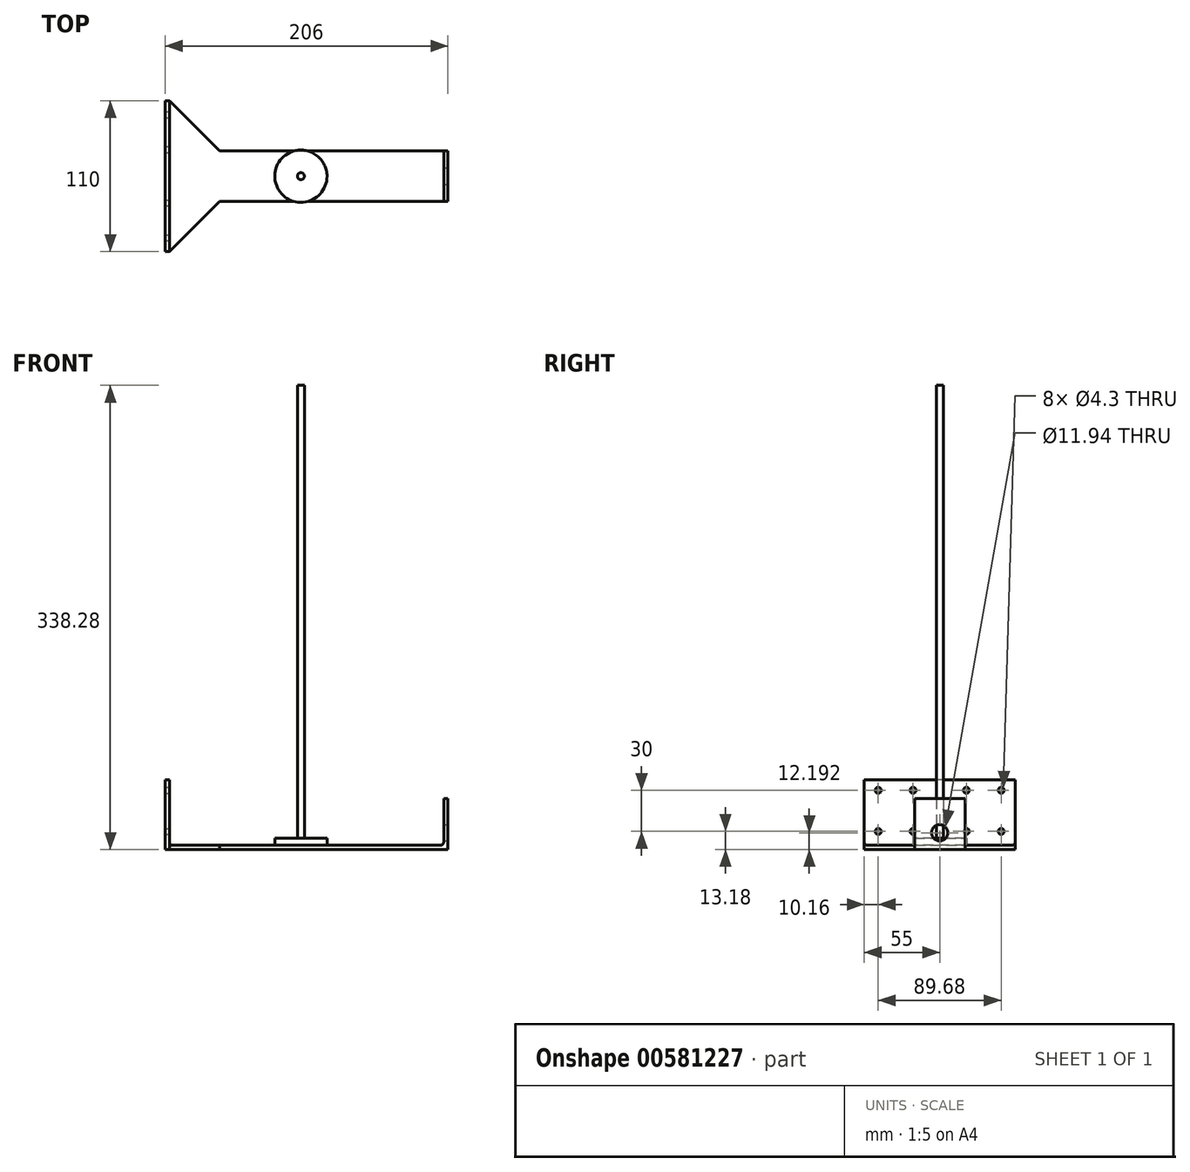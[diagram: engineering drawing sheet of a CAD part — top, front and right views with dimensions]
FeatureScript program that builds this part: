
annotation { "Feature Type Name" : "Feature", "Feature Type Description" : "" }
export const myFeature = defineFeature(function(context is Context, id is Id, definition is map)
    precondition{}
    {
        {
            var Q0;
            Q0=qCreatedBy(makeId("Top.planeOp"),FACE);
            var sketch = newSketch(context, id + "F0", { "sketchPlane" : qUnion([Q0])});
            skLineSegment(sketch, "E0.bottom", {"start": v(1.5, 55) * mm, "end": v(-1.5, 55) * mm});
            skLineSegment(sketch, "E0.top", {"start": v(1.5, -55) * mm, "end": v(-1.5, -55) * mm});
            skLineSegment(sketch, "E0.left", {"start": v(1.5, 55) * mm, "end": v(1.5, -55) * mm});
            skLineSegment(sketch, "E0.right", {"start": v(-1.5, 55) * mm, "end": v(-1.5, -55) * mm});
            skPoint(sketch, "E0.middle", {"position": v(0, 0) * mm});
            skLineSegment(sketch, "E1", {"start": v(1.5, 55) * mm, "end": v(38.09, 18.42) * mm});
            skLineSegment(sketch, "E2", {"start": v(1.5, -55) * mm, "end": v(38.09, -18.42) * mm});
            skLineSegment(sketch, "E3", {"start": v(38.09, 18.41) * mm, "end": v(201.5, 18.41) * mm});
            skLineSegment(sketch, "E4", {"start": v(38.09, -18.42) * mm, "end": v(201.5, -18.42) * mm});
            skLineSegment(sketch, "E5.bottom", {"start": v(201.5, 18.41) * mm, "end": v(204.5, 18.41) * mm});
            skLineSegment(sketch, "E5.top", {"start": v(201.5, -18.42) * mm, "end": v(204.5, -18.42) * mm});
            skLineSegment(sketch, "E5.left", {"start": v(201.5, 18.41) * mm, "end": v(201.5, -18.42) * mm});
            skLineSegment(sketch, "E5.right", {"start": v(204.5, 18.41) * mm, "end": v(204.5, -18.42) * mm});
            skSolve(sketch);
        }
        {
            var Q0;
            Q0=qSketchRegion(id+"F0",true);
            extrude(context, id + "F1", {"entities" : qUnion([Q0]), "depth" : 3 * mm, "offsetDistance" : 25.4 * mm});
        }
        {
            var Q0;
            Q0=makeQuery(id+"F0.imprint","IMPRINT",FACE,{"disambiguationData":[TD([[makeQuery(id+"F0.imprint","IMPRINT",EDGE,{"derivedFrom":sQuery(id+"F0.wireOp",EDGE,"E0.bottom")}),1.0]])]});
            extrude(context, id + "F2", {"entities" : qUnion([Q0]), "operationType" : NewBodyOperationType.ADD, "depth" : 50.8 * mm, "offsetDistance" : 25.4 * mm});
        }
        {
            var Q0;
            Q0=makeQuery(id+"F0.imprint","IMPRINT",FACE,{"disambiguationData":[TD([[makeQuery(id+"F0.imprint","IMPRINT",EDGE,{"derivedFrom":sQuery(id+"F0.wireOp",EDGE,"E5.bottom")}),-1.0]])]});
            extrude(context, id + "F3", {"entities" : qUnion([Q0]), "operationType" : NewBodyOperationType.ADD, "depth" : 37 * mm, "offsetDistance" : 25.4 * mm});
        }
        {
            var Q0;
            Q0=makeQuery(id+"F2.opExtrude","SWEPT_FACE",FACE,{"disambiguationData":[OSD([sQuery(id+"F0.wireOp",EDGE,"E0.left")])]});
            var sketch = newSketch(context, id + "F4", { "sketchPlane" : qUnion([Q0])});
            skCircle(sketch, "E6", {"center": v(-44.84, 43.18) * mm, "radius": 2.15 * mm});
            skCircle(sketch, "E7", {"center": v(-44.84, 13.18) * mm, "radius": 2.15 * mm});
            skCircle(sketch, "E8", {"center": v(-19.44, 43.18) * mm, "radius": 2.15 * mm});
            skCircle(sketch, "E9", {"center": v(-19.44, 13.18) * mm, "radius": 2.15 * mm});
            skCircle(sketch, "E10.MirrorC", {"center": v(44.84, 43.18) * mm, "radius": 2.15 * mm});
            skCircle(sketch, "E11.MirrorC", {"center": v(19.44, 43.18) * mm, "radius": 2.15 * mm});
            skCircle(sketch, "E12.MirrorC", {"center": v(19.44, 13.18) * mm, "radius": 2.15 * mm});
            skCircle(sketch, "E13.MirrorC", {"center": v(44.84, 13.18) * mm, "radius": 2.15 * mm});
            skSolve(sketch);
        }
        {
            var Q0;
            Q0=qSketchRegion(id+"F4",true);
            extrude(context, id + "F5", {"entities" : qUnion([Q0]), "operationType" : NewBodyOperationType.REMOVE, "oppositeDirection" : true, "depth" : 49.28 * mm, "offsetDistance" : 25.4 * mm});
        }
        {
            var Q0;
            {var subQ0=sQuery(id+"F0.wireOp",EDGE,"E5.right");Q0=makeQuery(id+"F3.boolean.opBoolean","MERGE",FACE,{"derivedFrom":[makeQuery(id+"F1.opExtrude","SWEPT_FACE",FACE,{"disambiguationData":[OSD([subQ0])]}),makeQuery(id+"F3.opExtrude","SWEPT_FACE",FACE,{"disambiguationData":[OSD([subQ0])]})]});}
            var sketch = newSketch(context, id + "F6", { "sketchPlane" : qUnion([Q0])});
            skCircle(sketch, "E14", {"center": v(0, 12.2) * mm, "radius": 5.97 * mm});
            skSolve(sketch);
        }
        {
            var Q0;
            Q0=qSketchRegion(id+"F6",true);
            extrude(context, id + "F7", {"entities" : qUnion([Q0]), "operationType" : NewBodyOperationType.REMOVE, "oppositeDirection" : true, "depth" : 38.1 * mm, "offsetDistance" : 25.4 * mm});
        }
        {
            var Q0;
            Q0=makeQuery(id+"F3.boolean.opBoolean","INTERSECT",EDGE,{"derivedFrom":[makeQuery(id+"F1.opExtrude","CAP_FACE",FACE,{"disambiguationData":[OSD([sQuery(id+"F0.wireOp",EDGE,"E0.bottom"),sQuery(id+"F0.wireOp",EDGE,"E0.top"),sQuery(id+"F0.wireOp",EDGE,"E0.right"),sQuery(id+"F0.wireOp",EDGE,"E1"),sQuery(id+"F0.wireOp",EDGE,"E2"),sQuery(id+"F0.wireOp",EDGE,"E3"),sQuery(id+"F0.wireOp",EDGE,"E4"),sQuery(id+"F0.wireOp",EDGE,"E5.bottom"),sQuery(id+"F0.wireOp",EDGE,"E5.top"),sQuery(id+"F0.wireOp",EDGE,"E5.right")])],"isStart":false}),makeQuery(id+"F3.opExtrude","SWEPT_FACE",FACE,{"disambiguationData":[OSD([sQuery(id+"F0.wireOp",EDGE,"E5.left")])]})]});
            fillet(context, id + "F8", {"entities" : qUnion([Q0]), "radius" : 2.54 * mm, "tangentPropagation" : true, "allowEdgeOverflow" : false});
        }
        {
            var Q0;
            Q0=makeQuery(id+"F1.opExtrude","CAP_FACE",FACE,{"disambiguationData":[OSD([sQuery(id+"F0.wireOp",EDGE,"E0.bottom"),sQuery(id+"F0.wireOp",EDGE,"E0.top"),sQuery(id+"F0.wireOp",EDGE,"E0.right"),sQuery(id+"F0.wireOp",EDGE,"E1"),sQuery(id+"F0.wireOp",EDGE,"E2"),sQuery(id+"F0.wireOp",EDGE,"E3"),sQuery(id+"F0.wireOp",EDGE,"E4"),sQuery(id+"F0.wireOp",EDGE,"E5.bottom"),sQuery(id+"F0.wireOp",EDGE,"E5.top"),sQuery(id+"F0.wireOp",EDGE,"E5.right")])],"isStart":false});
            var sketch = newSketch(context, id + "F9", { "sketchPlane" : qUnion([Q0])});
            skCircle(sketch, "E15", {"center": v(97.36, 0) * mm, "radius": 19.05 * mm});
            skSolve(sketch);
        }
        {
            var Q0;
            {var subQ0=sQuery(id+"F9.wireOp",EDGE,"E15");var subQ1=makeQuery(id+"F1.opExtrude","CAP_EDGE",EDGE,{"disambiguationData":[OSD([sQuery(id+"F0.wireOp",EDGE,"E4"),sQuery(id+"F0.wireOp",EDGE,"E5.top")])],"isStart":false});var subQ2=makeQuery(id+"F9.imprint","INTERSECT",VERTEX,{"disambiguationData":[OD(0.0)],"derivedFrom":[subQ1,subQ0]});Q0=makeQuery(id+"F9.imprint","IMPRINT",FACE,{"disambiguationData":[TD([[makeQuery(id+"F9.imprint","IMPRINT",EDGE,{"disambiguationData":[TD([[subQ2,-1.0]])],"derivedFrom":subQ0}),1.0]])]});}
            var Q1;
            {var subQ0=sQuery(id+"F9.wireOp",EDGE,"E15");var subQ1=makeQuery(id+"F1.opExtrude","CAP_EDGE",EDGE,{"disambiguationData":[OSD([sQuery(id+"F0.wireOp",EDGE,"E3"),sQuery(id+"F0.wireOp",EDGE,"E5.bottom")])],"isStart":false});var subQ2=makeQuery(id+"F9.imprint","INTERSECT",VERTEX,{"disambiguationData":[OD(0.0)],"derivedFrom":[subQ1,subQ0]});Q1=makeQuery(id+"F9.imprint","IMPRINT",FACE,{"disambiguationData":[TD([[makeQuery(id+"F9.imprint","IMPRINT",EDGE,{"disambiguationData":[TD([[subQ2,1.0]])],"derivedFrom":subQ0}),1.0]])]});}
            var Q2;
            {var subQ0=sQuery(id+"F9.wireOp",EDGE,"E15");var subQ1=makeQuery(id+"F1.opExtrude","CAP_EDGE",EDGE,{"disambiguationData":[OSD([sQuery(id+"F0.wireOp",EDGE,"E3"),sQuery(id+"F0.wireOp",EDGE,"E5.bottom")])],"isStart":false});var subQ2=makeQuery(id+"F9.imprint","INTERSECT",VERTEX,{"disambiguationData":[OD(0.0)],"derivedFrom":[subQ1,subQ0]});Q2=makeQuery(id+"F9.imprint","IMPRINT",FACE,{"disambiguationData":[TD([[makeQuery(id+"F9.imprint","IMPRINT",EDGE,{"disambiguationData":[TD([[subQ2,-1.0]])],"derivedFrom":subQ0}),1.0]])]});}
            extrude(context, id + "F10", {"entities" : qUnion([Q0, Q1, Q2]), "operationType" : NewBodyOperationType.ADD, "depth" : 5.08 * mm, "offsetDistance" : 25.4 * mm});
        }
        {
            var Q0;
            Q0=makeQuery(id+"F10.opExtrude","CAP_FACE",FACE,{"disambiguationData":[OSD([sQuery(id+"F9.wireOp",EDGE,"E15")])],"isStart":false});
            var sketch = newSketch(context, id + "F11", { "sketchPlane" : qUnion([Q0])});
            skCircle(sketch, "E16", {"center": v(97.36, 0) * mm, "radius": 2.54 * mm});
            skSolve(sketch);
        }
        {
            var Q0;
            Q0=makeQuery(id+"F11.imprint","IMPRINT",FACE,{"disambiguationData":[TD([[makeQuery(id+"F11.imprint","IMPRINT",EDGE,{"derivedFrom":sQuery(id+"F11.wireOp",EDGE,"E16")}),1.0]])]});
            extrude(context, id + "F12", {"entities" : qUnion([Q0]), "operationType" : NewBodyOperationType.ADD, "depth" : 330.2 * mm, "offsetDistance" : 25.4 * mm});
        }
        {
            var Q0;
            Q0=makeQuery(id+"F2.boolean.opBoolean","INTERSECT",EDGE,{"derivedFrom":[makeQuery(id+"F1.opExtrude","CAP_FACE",FACE,{"disambiguationData":[OSD([sQuery(id+"F0.wireOp",EDGE,"E0.bottom"),sQuery(id+"F0.wireOp",EDGE,"E0.top"),sQuery(id+"F0.wireOp",EDGE,"E0.right"),sQuery(id+"F0.wireOp",EDGE,"E1"),sQuery(id+"F0.wireOp",EDGE,"E2"),sQuery(id+"F0.wireOp",EDGE,"E3"),sQuery(id+"F0.wireOp",EDGE,"E4"),sQuery(id+"F0.wireOp",EDGE,"E5.bottom"),sQuery(id+"F0.wireOp",EDGE,"E5.top"),sQuery(id+"F0.wireOp",EDGE,"E5.right")])],"isStart":false}),makeQuery(id+"F2.opExtrude","SWEPT_FACE",FACE,{"disambiguationData":[OSD([sQuery(id+"F0.wireOp",EDGE,"E0.left")])]})]});
            fillet(context, id + "F13", {"entities" : qUnion([Q0]), "radius" : 2.54 * mm, "tangentPropagation" : true, "allowEdgeOverflow" : false});
        }
    });
